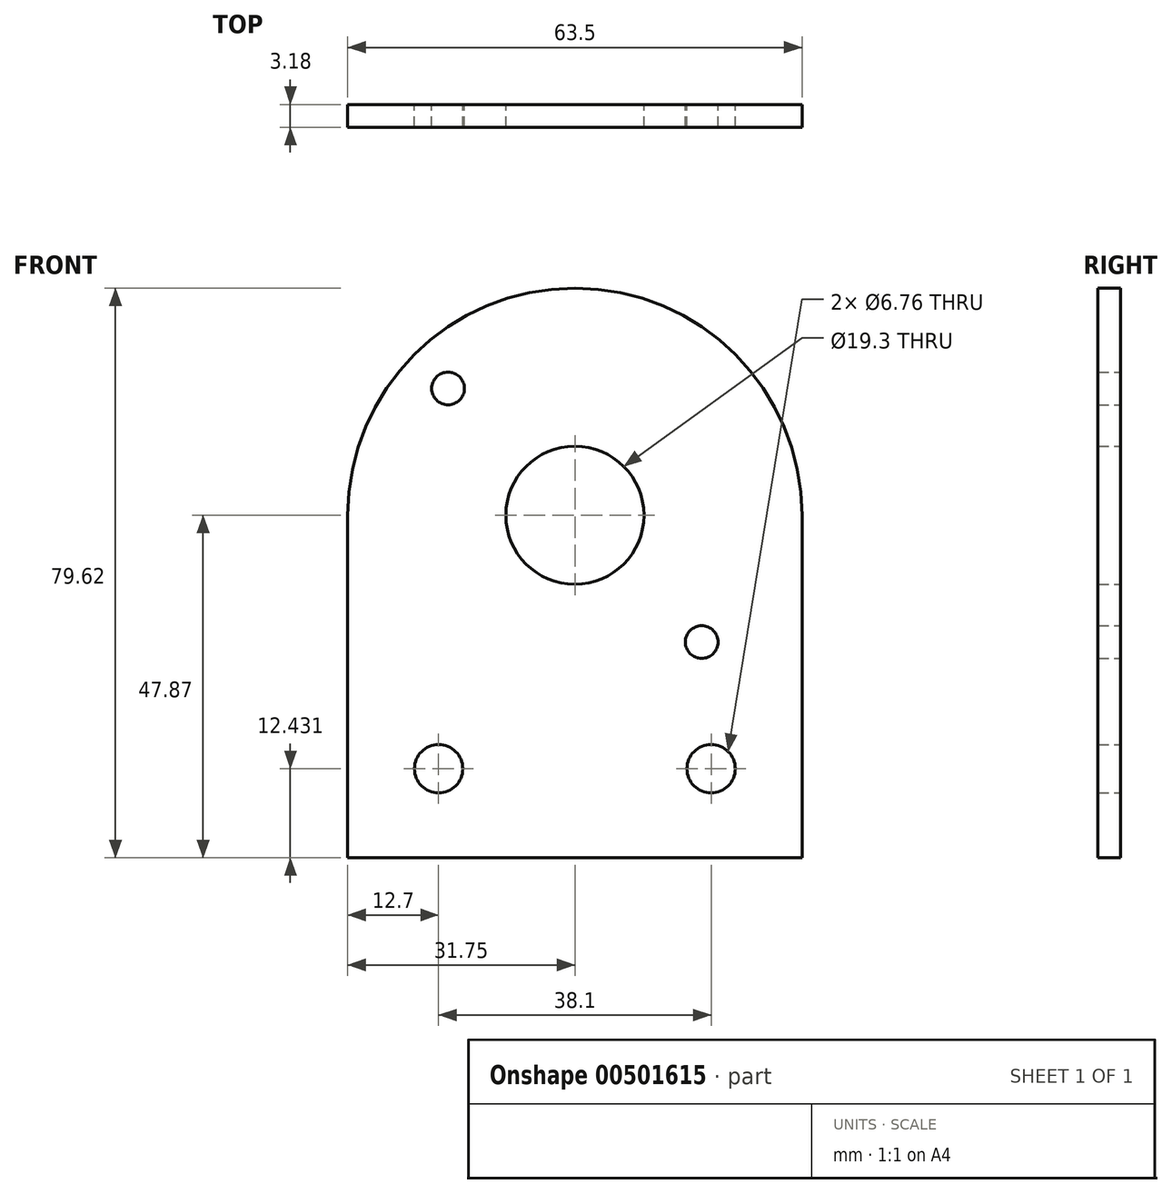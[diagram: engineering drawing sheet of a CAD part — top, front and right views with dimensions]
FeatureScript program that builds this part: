
annotation { "Feature Type Name" : "Feature", "Feature Type Description" : "" }
export const myFeature = defineFeature(function(context is Context, id is Id, definition is map)
    precondition{}
    {
        {
            var Q0;
            Q0=qCreatedBy(makeId("Front.planeOp"),FACE);
            var sketch = newSketch(context, id + "F0", { "sketchPlane" : qUnion([Q0])});
            skCircle(sketch, "E0", {"center": v(0, 0) * mm, "radius": 9.65 * mm});
            skLineSegment(sketch, "E1.bottom", {"start": v(17.73, -17.73) * mm, "end": v(-17.73, -17.73) * mm, "construction": true});
            skLineSegment(sketch, "E1.top", {"start": v(17.73, 17.73) * mm, "end": v(-17.73, 17.73) * mm, "construction": true});
            skLineSegment(sketch, "E1.left", {"start": v(17.73, -17.73) * mm, "end": v(17.73, 17.73) * mm, "construction": true});
            skLineSegment(sketch, "E1.right", {"start": v(-17.73, -17.73) * mm, "end": v(-17.73, 17.73) * mm, "construction": true});
            skCircle(sketch, "E2", {"center": v(-17.73, 17.73) * mm, "radius": 2.29 * mm});
            skCircle(sketch, "E3", {"center": v(17.73, -17.73) * mm, "radius": 2.29 * mm});
            skArc(sketch, "E4", {"start": v(31.75, 0) * mm, "mid": v(0, 31.75) * mm, "end": v(-31.75, 0) * mm});
            skLineSegment(sketch, "E5.bottom", {"start": v(31.75, -47.87) * mm, "end": v(-31.75, -47.87) * mm});
            skLineSegment(sketch, "E5.left", {"start": v(31.75, -47.87) * mm, "end": v(31.75, -15.63) * mm});
            skLineSegment(sketch, "E5.right", {"start": v(-31.75, -47.87) * mm, "end": v(-31.75, -15.63) * mm});
            skPoint(sketch, "E5.middle", {"position": v(0, -31.75) * mm});
            skLineSegment(sketch, "E6", {"start": v(-31.75, -15.63) * mm, "end": v(-31.75, 0) * mm});
            skLineSegment(sketch, "E7", {"start": v(31.75, -15.63) * mm, "end": v(31.75, 0) * mm});
            skLineSegment(sketch, "E8", {"start": v(-19.05, -47.87) * mm, "end": v(-19.05, -35.44) * mm, "construction": true});
            skLineSegment(sketch, "E9", {"start": v(-31.75, -35.44) * mm, "end": v(-19.05, -35.44) * mm, "construction": true});
            skLineSegment(sketch, "E10.MirrorCS", {"start": v(31.75, -35.44) * mm, "end": v(19.05, -35.44) * mm, "construction": true});
            skLineSegment(sketch, "E11.MirrorCS", {"start": v(19.05, -47.87) * mm, "end": v(19.05, -35.44) * mm, "construction": true});
            skCircle(sketch, "E12", {"center": v(-19.05, -35.44) * mm, "radius": 3.38 * mm});
            skCircle(sketch, "E13.MirrorC", {"center": v(19.05, -35.44) * mm, "radius": 3.38 * mm});
            skSolve(sketch);
        }
        {
            var Q0;
            Q0=makeQuery(id+"F0.imprint","IMPRINT",FACE,{"disambiguationData":[TD([[makeQuery(id+"F0.imprint","IMPRINT",EDGE,{"derivedFrom":sQuery(id+"F0.wireOp",EDGE,"E0")}),-1.0]])]});
            extrude(context, id + "F1", {"entities" : qUnion([Q0]), "depth" : 3.17 * mm, "offsetDistance" : 25.4 * mm});
        }
    });
